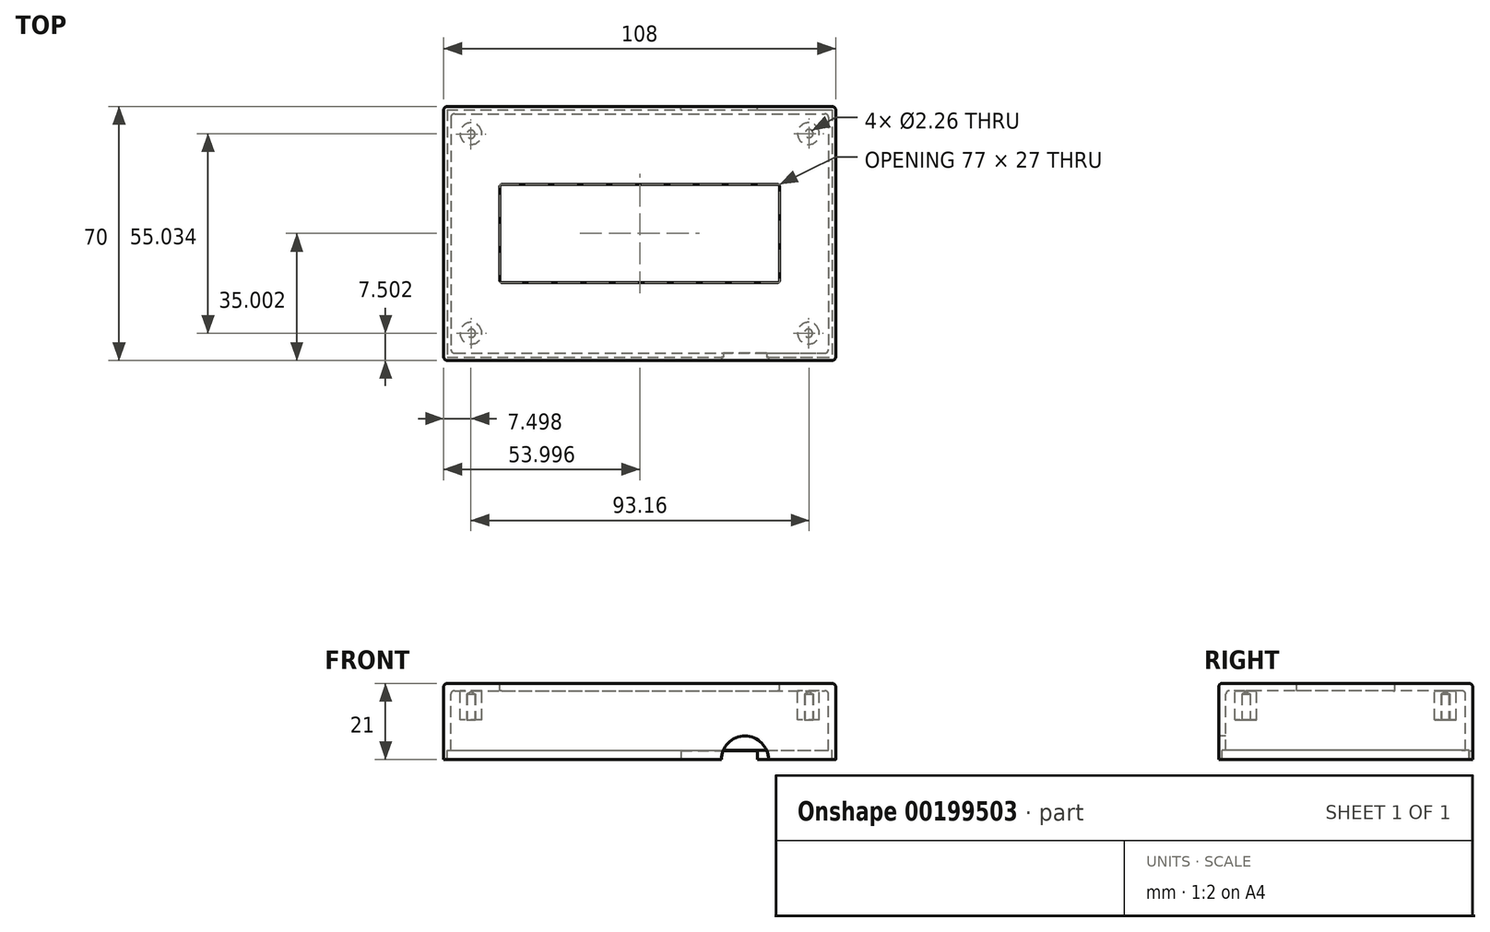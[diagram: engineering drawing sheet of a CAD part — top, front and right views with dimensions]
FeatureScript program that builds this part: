
annotation { "Feature Type Name" : "Feature", "Feature Type Description" : "" }
export const myFeature = defineFeature(function(context is Context, id is Id, definition is map)
    precondition{}
    {
        {
            var Q0;
            Q0=qCreatedBy(makeId("Top.planeOp"),FACE);
            var sketch = newSketch(context, id + "F0", { "sketchPlane" : qUnion([Q0])});
            skLineSegment(sketch, "E0.bottom", {"start": v(-57.35, 34.9) * mm, "end": v(50.65, 34.9) * mm});
            skLineSegment(sketch, "E0.top", {"start": v(-57.35, -35.1) * mm, "end": v(50.65, -35.1) * mm});
            skLineSegment(sketch, "E0.left", {"start": v(-57.35, 34.9) * mm, "end": v(-57.35, -35.1) * mm});
            skLineSegment(sketch, "E0.right", {"start": v(50.65, 34.9) * mm, "end": v(50.65, -35.1) * mm});
            skLineSegment(sketch, "E1.bottom", {"start": v(-41.35, 13.4) * mm, "end": v(34.65, 13.4) * mm});
            skLineSegment(sketch, "E1.top", {"start": v(-41.35, -13.6) * mm, "end": v(34.65, -13.6) * mm});
            skLineSegment(sketch, "E1.left", {"start": v(-41.85, 12.9) * mm, "end": v(-41.85, -13.1) * mm});
            skLineSegment(sketch, "E1.right", {"start": v(35.15, 12.9) * mm, "end": v(35.15, -13.1) * mm});
            skLineSegment(sketch, "E2.bottom", {"start": v(-55.35, 32.9) * mm, "end": v(48.65, 32.9) * mm});
            skLineSegment(sketch, "E2.top", {"start": v(-55.35, -33.1) * mm, "end": v(48.65, -33.1) * mm});
            skLineSegment(sketch, "E2.left", {"start": v(-55.35, 32.9) * mm, "end": v(-55.35, -33.1) * mm});
            skLineSegment(sketch, "E2.right", {"start": v(48.65, 32.9) * mm, "end": v(48.65, -33.1) * mm});
            skCircle(sketch, "E3", {"center": v(-49.85, 27.4) * mm, "radius": 3 * mm});
            skCircle(sketch, "E4", {"center": v(43.15, 27.4) * mm, "radius": 3 * mm});
            skCircle(sketch, "E5", {"center": v(-49.85, -27.6) * mm, "radius": 3 * mm});
            skCircle(sketch, "E6", {"center": v(43.15, -27.6) * mm, "radius": 3 * mm});
            skPoint(sketch, "E7.visualSharp", {"position": v(-55.35, -33.1) * mm});
            skPoint(sketch, "E8.visualSharp", {"position": v(-55.35, 32.9) * mm});
            skPoint(sketch, "E9.visualSharp", {"position": v(48.65, 32.9) * mm});
            skPoint(sketch, "E10.visualSharp", {"position": v(48.65, -33.1) * mm});
            skPoint(sketch, "E11.visualSharp", {"position": v(-57.35, 34.9) * mm});
            skPoint(sketch, "E12.visualSharp", {"position": v(50.65, 34.9) * mm});
            skPoint(sketch, "E13.visualSharp", {"position": v(50.65, -35.1) * mm});
            skLineSegment(sketch, "E14.bottom", {"start": v(-56.4, 33.94) * mm, "end": v(49.7, 33.94) * mm});
            skLineSegment(sketch, "E14.top", {"start": v(-56.4, -34.16) * mm, "end": v(49.7, -34.16) * mm});
            skLineSegment(sketch, "E14.left", {"start": v(-56.4, 33.94) * mm, "end": v(-56.4, -34.16) * mm});
            skLineSegment(sketch, "E14.right", {"start": v(49.7, 33.94) * mm, "end": v(49.7, -34.16) * mm});
            skPoint(sketch, "E15.visualSharp", {"position": v(-41.85, 13.4) * mm});
            skArc(sketch, "E15.filletArc", {"start": v(-41.35, 13.4) * mm, "mid": v(-41.7, 13.25) * mm, "end": v(-41.85, 12.9) * mm});
            skPoint(sketch, "E16.visualSharp", {"position": v(35.15, 13.4) * mm});
            skArc(sketch, "E16.filletArc", {"start": v(35.15, 12.9) * mm, "mid": v(35, 13.25) * mm, "end": v(34.65, 13.4) * mm});
            skPoint(sketch, "E17.visualSharp", {"position": v(35.15, -13.6) * mm});
            skArc(sketch, "E17.filletArc", {"start": v(34.65, -13.6) * mm, "mid": v(35, -13.46) * mm, "end": v(35.15, -13.1) * mm});
            skPoint(sketch, "E18.visualSharp", {"position": v(-41.85, -13.6) * mm});
            skArc(sketch, "E18.filletArc", {"start": v(-41.85, -13.1) * mm, "mid": v(-41.7, -13.46) * mm, "end": v(-41.35, -13.6) * mm});
            skSolve(sketch);
        }
        {
            var Q0;
            Q0=makeQuery(id+"F0.imprint","IMPRINT",FACE,{"disambiguationData":[TD([[makeQuery(id+"F0.imprint","IMPRINT",EDGE,{"derivedFrom":sQuery(id+"F0.wireOp",EDGE,"E2.bottom")}),1.0]])]});
            var Q1;
            Q1=makeQuery(id+"F0.imprint","IMPRINT",FACE,{"disambiguationData":[TD([[makeQuery(id+"F0.imprint","IMPRINT",EDGE,{"derivedFrom":sQuery(id+"F0.wireOp",EDGE,"E2.bottom")}),-1.0]])]});
            var Q2;
            Q2=makeQuery(id+"F0.imprint","IMPRINT",FACE,{"disambiguationData":[TD([[makeQuery(id+"F0.imprint","IMPRINT",EDGE,{"derivedFrom":sQuery(id+"F0.wireOp",EDGE,"E3")}),1.0]])]});
            var Q3;
            Q3=makeQuery(id+"F0.imprint","IMPRINT",FACE,{"disambiguationData":[TD([[makeQuery(id+"F0.imprint","IMPRINT",EDGE,{"derivedFrom":sQuery(id+"F0.wireOp",EDGE,"E4")}),1.0]])]});
            var Q4;
            Q4=makeQuery(id+"F0.imprint","IMPRINT",FACE,{"disambiguationData":[TD([[makeQuery(id+"F0.imprint","IMPRINT",EDGE,{"derivedFrom":sQuery(id+"F0.wireOp",EDGE,"E6")}),1.0]])]});
            var Q5;
            Q5=makeQuery(id+"F0.imprint","IMPRINT",FACE,{"disambiguationData":[TD([[makeQuery(id+"F0.imprint","IMPRINT",EDGE,{"derivedFrom":sQuery(id+"F0.wireOp",EDGE,"E5")}),1.0]])]});
            var Q6;
            Q6=makeQuery(id+"F0.imprint","IMPRINT",FACE,{"disambiguationData":[TD([[makeQuery(id+"F0.imprint","IMPRINT",EDGE,{"derivedFrom":sQuery(id+"F0.wireOp",EDGE,"E0.bottom")}),-1.0]])]});
            extrude(context, id + "F1", {"entities" : qUnion([Q0, Q1, Q2, Q3, Q4, Q5, Q6]), "oppositeDirection" : true, "depth" : 2 * mm});
        }
        {
            var Q0;
            Q0=makeQuery(id+"F0.imprint","IMPRINT",FACE,{"disambiguationData":[TD([[makeQuery(id+"F0.imprint","IMPRINT",EDGE,{"derivedFrom":sQuery(id+"F0.wireOp",EDGE,"E2.bottom")}),1.0]])]});
            extrude(context, id + "F2", {"entities" : qUnion([Q0]), "operationType" : NewBodyOperationType.ADD, "oppositeDirection" : true, "depth" : 18.49 * mm});
        }
        {
            var Q0;
            {var subQ0=sQuery(id+"F0.wireOp",EDGE,"E0.right");var subQ1=sQuery(id+"F0.wireOp",EDGE,"E0.left");var subQ2=sQuery(id+"F0.wireOp",EDGE,"E0.top");var subQ3=sQuery(id+"F0.wireOp",EDGE,"E0.bottom");Q0=makeQuery(id+"F2.boolean.opBoolean","SPLIT",FACE,{"disambiguationData":[TD([makeQuery(id+"F1.opExtrude","SWEPT_FACE",FACE,{"disambiguationData":[OSD([subQ3])]})])],"derivedFrom":makeQuery(id+"F1.opExtrude","CAP_FACE",FACE,{"disambiguationData":[OSD([subQ3,subQ2,subQ1,subQ0,sQuery(id+"F0.wireOp",EDGE,"E1.bottom"),sQuery(id+"F0.wireOp",EDGE,"E1.top"),sQuery(id+"F0.wireOp",EDGE,"E1.left"),sQuery(id+"F0.wireOp",EDGE,"E1.right"),sQuery(id+"F0.wireOp",EDGE,"TIqVLyNP-uRYi-IZCg-FFMY-wpAB1gUjtPzc"),sQuery(id+"F0.wireOp",EDGE,"eGpXYtko-bpSR-Pbzy-FSSL-hkfkqHyOyQKH"),sQuery(id+"F0.wireOp",EDGE,"aKAKSCUs-jV2O-gDTW-lYoO-wS98vJuitCCh"),sQuery(id+"F0.wireOp",EDGE,"Y9MBlFMN-f0e3-QmNQ-qzjT-em0skZvg3ODU")])],"isStart":false})});}
            extrude(context, id + "F3", {"entities" : qUnion([Q0]), "operationType" : NewBodyOperationType.ADD, "depth" : 19 * mm});
        }
        {
            var Q0;
            Q0=makeQuery(id+"F0.imprint","IMPRINT",FACE,{"disambiguationData":[TD([[makeQuery(id+"F0.imprint","IMPRINT",EDGE,{"derivedFrom":sQuery(id+"F0.wireOp",EDGE,"E3")}),1.0]])]});
            var Q1;
            Q1=makeQuery(id+"F0.imprint","IMPRINT",FACE,{"disambiguationData":[TD([[makeQuery(id+"F0.imprint","IMPRINT",EDGE,{"derivedFrom":sQuery(id+"F0.wireOp",EDGE,"E4")}),1.0]])]});
            var Q2;
            Q2=makeQuery(id+"F0.imprint","IMPRINT",FACE,{"disambiguationData":[TD([[makeQuery(id+"F0.imprint","IMPRINT",EDGE,{"derivedFrom":sQuery(id+"F0.wireOp",EDGE,"E5")}),1.0]])]});
            var Q3;
            Q3=makeQuery(id+"F0.imprint","IMPRINT",FACE,{"disambiguationData":[TD([[makeQuery(id+"F0.imprint","IMPRINT",EDGE,{"derivedFrom":sQuery(id+"F0.wireOp",EDGE,"E6")}),1.0]])]});
            extrude(context, id + "F4", {"entities" : qUnion([Q0, Q1, Q2, Q3]), "operationType" : NewBodyOperationType.ADD, "oppositeDirection" : true, "depth" : 10 * mm});
        }
        {
            var Q0;
            {var subQ0=sQuery(id+"F0.wireOp",EDGE,"E0.top");Q0=makeQuery(id+"F3.boolean.opBoolean","MERGE",FACE,{"derivedFrom":[makeQuery(id+"F1.opExtrude","SWEPT_FACE",FACE,{"disambiguationData":[OSD([subQ0])]}),makeQuery(id+"F3.opExtrude","SWEPT_FACE",FACE,{"disambiguationData":[OSD([subQ0])]})]});}
            var sketch = newSketch(context, id + "F5", { "sketchPlane" : qUnion([Q0])});
            skPoint(sketch, "E19", {"position": v(25.65, -21) * mm});
            skCircle(sketch, "E20", {"center": v(25.65, -21) * mm, "radius": 6.5 * mm});
            skSolve(sketch);
        }
        {
            var Q0;
            {var subQ0=sQuery(id+"F5.wireOp",EDGE,"E20");var subQ1=makeQuery(id+"F3.opExtrude","CAP_EDGE",EDGE,{"disambiguationData":[OSD([sQuery(id+"F0.wireOp",EDGE,"E0.top")])],"isStart":false});var subQ2=makeQuery(id+"F5.imprint","INTERSECT",VERTEX,{"disambiguationData":[OD(0.0)],"derivedFrom":[subQ1,subQ0]});Q0=makeQuery(id+"F5.imprint","IMPRINT",FACE,{"disambiguationData":[TD([[makeQuery(id+"F5.imprint","IMPRINT",EDGE,{"disambiguationData":[TD([[subQ2,1.0]])],"derivedFrom":subQ0}),1.0]])]});}
            extrude(context, id + "F6", {"entities" : qUnion([Q0]), "operationType" : NewBodyOperationType.REMOVE, "oppositeDirection" : true, "depth" : 2.5 * mm});
        }
        {
            var Q0;
            {var subQ0=sQuery(id+"F0.wireOp",EDGE,"E0.bottom");Q0=makeQuery(id+"F3.boolean.opBoolean","MERGE",FACE,{"derivedFrom":[makeQuery(id+"F1.opExtrude","SWEPT_FACE",FACE,{"disambiguationData":[OSD([subQ0])]}),makeQuery(id+"F3.opExtrude","SWEPT_FACE",FACE,{"disambiguationData":[OSD([subQ0])]})]});}
            var sketch = newSketch(context, id + "F7", { "sketchPlane" : qUnion([Q0])});
            skLineSegment(sketch, "E21.bottom", {"start": v(-29.05, -21) * mm, "end": v(-8.05, -21) * mm});
            skLineSegment(sketch, "E21.top", {"start": v(-29.05, -18.6) * mm, "end": v(-8.05, -18.6) * mm});
            skLineSegment(sketch, "E21.left", {"start": v(-29.05, -21) * mm, "end": v(-29.05, -18.6) * mm});
            skLineSegment(sketch, "E21.right", {"start": v(-8.05, -21) * mm, "end": v(-8.05, -18.6) * mm});
            skSolve(sketch);
        }
        {
            var Q0;
            Q0=makeQuery(id+"F7.imprint","IMPRINT",FACE,{"disambiguationData":[TD([[makeQuery(id+"F7.imprint","IMPRINT",EDGE,{"derivedFrom":sQuery(id+"F7.wireOp",EDGE,"E21.bottom")}),-1.0]])]});
            extrude(context, id + "F8", {"entities" : qUnion([Q0]), "operationType" : NewBodyOperationType.REMOVE, "oppositeDirection" : true, "depth" : 2.5 * mm});
        }
        {
            var Q0;
            Q0=makeQuery(id+"F4.opExtrude","CAP_FACE",FACE,{"disambiguationData":[OSD([sQuery(id+"F0.wireOp",EDGE,"E6")])],"isStart":false});
            var sketch = newSketch(context, id + "F9", { "sketchPlane" : qUnion([Q0])});
            skPoint(sketch, "E22", {"position": v(-49.85, -27.23) * mm});
            skPoint(sketch, "E23", {"position": v(43.3, -27.43) * mm});
            skPoint(sketch, "E24", {"position": v(43.15, 27.6) * mm});
            skPoint(sketch, "E25", {"position": v(-49.73, 27.6) * mm});
            skSolve(sketch);
        }
        {
            var Q0;
            Q0=sQuery(id+"F9.wireOp",VERTEX,"E22");
            var Q1;
            Q1=sQuery(id+"F9.wireOp",VERTEX,"E23");
            var Q2;
            Q2=sQuery(id+"F9.wireOp",VERTEX,"E24");
            var Q3;
            Q3=sQuery(id+"F9.wireOp",VERTEX,"E25");
            var Q4;
            Q4=makeQuery(id+"F1.opExtrude","SWEPT_BODY",BODY,{"disambiguationData":[OSD([sQuery(id+"F0.wireOp",EDGE,"E0.bottom"),sQuery(id+"F0.wireOp",EDGE,"E0.top"),sQuery(id+"F0.wireOp",EDGE,"E0.left"),sQuery(id+"F0.wireOp",EDGE,"E0.right"),sQuery(id+"F0.wireOp",EDGE,"E1.bottom"),sQuery(id+"F0.wireOp",EDGE,"E1.top"),sQuery(id+"F0.wireOp",EDGE,"E1.left"),sQuery(id+"F0.wireOp",EDGE,"E1.right"),sQuery(id+"F0.wireOp",EDGE,"TIqVLyNP-uRYi-IZCg-FFMY-wpAB1gUjtPzc"),sQuery(id+"F0.wireOp",EDGE,"eGpXYtko-bpSR-Pbzy-FSSL-hkfkqHyOyQKH"),sQuery(id+"F0.wireOp",EDGE,"aKAKSCUs-jV2O-gDTW-lYoO-wS98vJuitCCh"),sQuery(id+"F0.wireOp",EDGE,"Y9MBlFMN-f0e3-QmNQ-qzjT-em0skZvg3ODU")])]});
            hole(context, id + "F10", {"style" : HoleStyle.SIMPLE, "endStyle" : HoleEndStyle.BLIND, "standardTappedOrClearance" : lookupTablePath({ "standard" : "ANSI", "size" : "#43 (0.09)", "type" : "Drilled" }), "standardBlindInLast" : lookupTablePath({ "standard" : "ANSI", "size" : "#43", "type" : "Drilled" }), "holeDiameter" : 2.26 * mm, "holeDepth" : 7 * mm, "tappedDepth" : 12 * mm, "tapClearance" : 3, "startFromSketch" : true, "locations" : qUnion([Q0, Q1, Q2, Q3]), "scope" : qUnion([Q4])});
        }
        {
            var Q0;
            Q0=makeQuery(id+"F1.opExtrude","CAP_EDGE",EDGE,{"disambiguationData":[OSD([sQuery(id+"F0.wireOp",EDGE,"E0.left")])],"isStart":true});
            var Q1;
            Q1=makeQuery(id+"F1.opExtrude","CAP_EDGE",EDGE,{"disambiguationData":[OSD([sQuery(id+"F0.wireOp",EDGE,"E0.bottom")])],"isStart":true});
            var Q2;
            Q2=makeQuery(id+"F1.opExtrude","CAP_EDGE",EDGE,{"disambiguationData":[OSD([sQuery(id+"F0.wireOp",EDGE,"E0.right")])],"isStart":true});
            var Q3;
            {var subQ0=sQuery(id+"F0.wireOp",EDGE,"E0.right");var subQ1=sQuery(id+"F0.wireOp",EDGE,"E0.top");Q3=makeQuery(id+"F3.boolean.opBoolean","MERGE",EDGE,{"derivedFrom":[makeQuery(id+"F1.opExtrude","SWEPT_EDGE",EDGE,{"disambiguationData":[OSD([subQ1,subQ0])]}),makeQuery(id+"F3.opExtrude","SWEPT_EDGE",EDGE,{"disambiguationData":[OSD([subQ1,subQ0])]})]});}
            var Q4;
            Q4=makeQuery(id+"F1.opExtrude","CAP_EDGE",EDGE,{"disambiguationData":[OSD([sQuery(id+"F0.wireOp",EDGE,"E0.top")])],"isStart":true});
            var Q5;
            {var subQ0=sQuery(id+"F0.wireOp",EDGE,"E0.left");var subQ1=sQuery(id+"F0.wireOp",EDGE,"E0.top");Q5=makeQuery(id+"F3.boolean.opBoolean","MERGE",EDGE,{"derivedFrom":[makeQuery(id+"F1.opExtrude","SWEPT_EDGE",EDGE,{"disambiguationData":[OSD([subQ1,subQ0])]}),makeQuery(id+"F3.opExtrude","SWEPT_EDGE",EDGE,{"disambiguationData":[OSD([subQ1,subQ0])]})]});}
            var Q6;
            {var subQ0=sQuery(id+"F0.wireOp",EDGE,"E0.right");var subQ1=sQuery(id+"F0.wireOp",EDGE,"E0.bottom");Q6=makeQuery(id+"F3.boolean.opBoolean","MERGE",EDGE,{"derivedFrom":[makeQuery(id+"F1.opExtrude","SWEPT_EDGE",EDGE,{"disambiguationData":[OSD([subQ1,subQ0])]}),makeQuery(id+"F3.opExtrude","SWEPT_EDGE",EDGE,{"disambiguationData":[OSD([subQ1,subQ0])]})]});}
            var Q7;
            {var subQ0=sQuery(id+"F0.wireOp",EDGE,"E0.left");var subQ1=sQuery(id+"F0.wireOp",EDGE,"E0.bottom");Q7=makeQuery(id+"F3.boolean.opBoolean","MERGE",EDGE,{"derivedFrom":[makeQuery(id+"F1.opExtrude","SWEPT_EDGE",EDGE,{"disambiguationData":[OSD([subQ1,subQ0])]}),makeQuery(id+"F3.opExtrude","SWEPT_EDGE",EDGE,{"disambiguationData":[OSD([subQ1,subQ0])]})]});}
            fillet(context, id + "F11", {"entities" : qUnion([Q0, Q1, Q2, Q3, Q4, Q5, Q6, Q7]), "radius" : 1 * mm, "tangentPropagation" : true, "allowEdgeOverflow" : false});
        }
        {
            var Q0;
            Q0=makeQuery(id+"F2.opExtrude","SWEPT_EDGE",EDGE,{"disambiguationData":[OSD([sQuery(id+"F0.wireOp",EDGE,"E2.top"),sQuery(id+"F0.wireOp",EDGE,"E2.right")])]});
            var Q1;
            Q1=makeQuery(id+"F2.boolean.opBoolean","INTERSECT",EDGE,{"derivedFrom":[makeQuery(id+"F1.opExtrude","CAP_FACE",FACE,{"disambiguationData":[OSD([sQuery(id+"F0.wireOp",EDGE,"E0.bottom"),sQuery(id+"F0.wireOp",EDGE,"E0.top"),sQuery(id+"F0.wireOp",EDGE,"E0.left"),sQuery(id+"F0.wireOp",EDGE,"E0.right"),sQuery(id+"F0.wireOp",EDGE,"E1.bottom"),sQuery(id+"F0.wireOp",EDGE,"E1.top"),sQuery(id+"F0.wireOp",EDGE,"E1.left"),sQuery(id+"F0.wireOp",EDGE,"E1.right"),sQuery(id+"F0.wireOp",EDGE,"TIqVLyNP-uRYi-IZCg-FFMY-wpAB1gUjtPzc"),sQuery(id+"F0.wireOp",EDGE,"eGpXYtko-bpSR-Pbzy-FSSL-hkfkqHyOyQKH"),sQuery(id+"F0.wireOp",EDGE,"aKAKSCUs-jV2O-gDTW-lYoO-wS98vJuitCCh"),sQuery(id+"F0.wireOp",EDGE,"Y9MBlFMN-f0e3-QmNQ-qzjT-em0skZvg3ODU")])],"isStart":false}),makeQuery(id+"F2.opExtrude","SWEPT_FACE",FACE,{"disambiguationData":[OSD([sQuery(id+"F0.wireOp",EDGE,"E2.right")])]})]});
            var Q2;
            Q2=makeQuery(id+"F2.boolean.opBoolean","INTERSECT",EDGE,{"derivedFrom":[makeQuery(id+"F1.opExtrude","CAP_FACE",FACE,{"disambiguationData":[OSD([sQuery(id+"F0.wireOp",EDGE,"E0.bottom"),sQuery(id+"F0.wireOp",EDGE,"E0.top"),sQuery(id+"F0.wireOp",EDGE,"E0.left"),sQuery(id+"F0.wireOp",EDGE,"E0.right"),sQuery(id+"F0.wireOp",EDGE,"E1.bottom"),sQuery(id+"F0.wireOp",EDGE,"E1.top"),sQuery(id+"F0.wireOp",EDGE,"E1.left"),sQuery(id+"F0.wireOp",EDGE,"E1.right"),sQuery(id+"F0.wireOp",EDGE,"TIqVLyNP-uRYi-IZCg-FFMY-wpAB1gUjtPzc"),sQuery(id+"F0.wireOp",EDGE,"eGpXYtko-bpSR-Pbzy-FSSL-hkfkqHyOyQKH"),sQuery(id+"F0.wireOp",EDGE,"aKAKSCUs-jV2O-gDTW-lYoO-wS98vJuitCCh"),sQuery(id+"F0.wireOp",EDGE,"Y9MBlFMN-f0e3-QmNQ-qzjT-em0skZvg3ODU")])],"isStart":false}),makeQuery(id+"F2.opExtrude","SWEPT_FACE",FACE,{"disambiguationData":[OSD([sQuery(id+"F0.wireOp",EDGE,"E2.top")])]})]});
            var Q3;
            Q3=makeQuery(id+"F2.opExtrude","SWEPT_EDGE",EDGE,{"disambiguationData":[OSD([sQuery(id+"F0.wireOp",EDGE,"E2.top"),sQuery(id+"F0.wireOp",EDGE,"E2.left")])]});
            var Q4;
            Q4=makeQuery(id+"F2.boolean.opBoolean","INTERSECT",EDGE,{"derivedFrom":[makeQuery(id+"F1.opExtrude","CAP_FACE",FACE,{"disambiguationData":[OSD([sQuery(id+"F0.wireOp",EDGE,"E0.bottom"),sQuery(id+"F0.wireOp",EDGE,"E0.top"),sQuery(id+"F0.wireOp",EDGE,"E0.left"),sQuery(id+"F0.wireOp",EDGE,"E0.right"),sQuery(id+"F0.wireOp",EDGE,"E1.bottom"),sQuery(id+"F0.wireOp",EDGE,"E1.top"),sQuery(id+"F0.wireOp",EDGE,"E1.left"),sQuery(id+"F0.wireOp",EDGE,"E1.right"),sQuery(id+"F0.wireOp",EDGE,"TIqVLyNP-uRYi-IZCg-FFMY-wpAB1gUjtPzc"),sQuery(id+"F0.wireOp",EDGE,"eGpXYtko-bpSR-Pbzy-FSSL-hkfkqHyOyQKH"),sQuery(id+"F0.wireOp",EDGE,"aKAKSCUs-jV2O-gDTW-lYoO-wS98vJuitCCh"),sQuery(id+"F0.wireOp",EDGE,"Y9MBlFMN-f0e3-QmNQ-qzjT-em0skZvg3ODU")])],"isStart":false}),makeQuery(id+"F2.opExtrude","SWEPT_FACE",FACE,{"disambiguationData":[OSD([sQuery(id+"F0.wireOp",EDGE,"E2.left")])]})]});
            var Q5;
            Q5=makeQuery(id+"F2.opExtrude","SWEPT_EDGE",EDGE,{"disambiguationData":[OSD([sQuery(id+"F0.wireOp",EDGE,"E2.bottom"),sQuery(id+"F0.wireOp",EDGE,"E2.left")])]});
            var Q6;
            Q6=makeQuery(id+"F2.boolean.opBoolean","INTERSECT",EDGE,{"derivedFrom":[makeQuery(id+"F1.opExtrude","CAP_FACE",FACE,{"disambiguationData":[OSD([sQuery(id+"F0.wireOp",EDGE,"E0.bottom"),sQuery(id+"F0.wireOp",EDGE,"E0.top"),sQuery(id+"F0.wireOp",EDGE,"E0.left"),sQuery(id+"F0.wireOp",EDGE,"E0.right"),sQuery(id+"F0.wireOp",EDGE,"E1.bottom"),sQuery(id+"F0.wireOp",EDGE,"E1.top"),sQuery(id+"F0.wireOp",EDGE,"E1.left"),sQuery(id+"F0.wireOp",EDGE,"E1.right"),sQuery(id+"F0.wireOp",EDGE,"TIqVLyNP-uRYi-IZCg-FFMY-wpAB1gUjtPzc"),sQuery(id+"F0.wireOp",EDGE,"eGpXYtko-bpSR-Pbzy-FSSL-hkfkqHyOyQKH"),sQuery(id+"F0.wireOp",EDGE,"aKAKSCUs-jV2O-gDTW-lYoO-wS98vJuitCCh"),sQuery(id+"F0.wireOp",EDGE,"Y9MBlFMN-f0e3-QmNQ-qzjT-em0skZvg3ODU")])],"isStart":false}),makeQuery(id+"F2.opExtrude","SWEPT_FACE",FACE,{"disambiguationData":[OSD([sQuery(id+"F0.wireOp",EDGE,"E2.bottom")])]})]});
            var Q7;
            Q7=makeQuery(id+"F2.opExtrude","SWEPT_EDGE",EDGE,{"disambiguationData":[OSD([sQuery(id+"F0.wireOp",EDGE,"E2.bottom"),sQuery(id+"F0.wireOp",EDGE,"E2.right")])]});
            fillet(context, id + "F12", {"entities" : qUnion([Q0, Q1, Q2, Q3, Q4, Q5, Q6, Q7]), "radius" : 1 * mm, "tangentPropagation" : true, "allowEdgeOverflow" : false});
        }
    });
